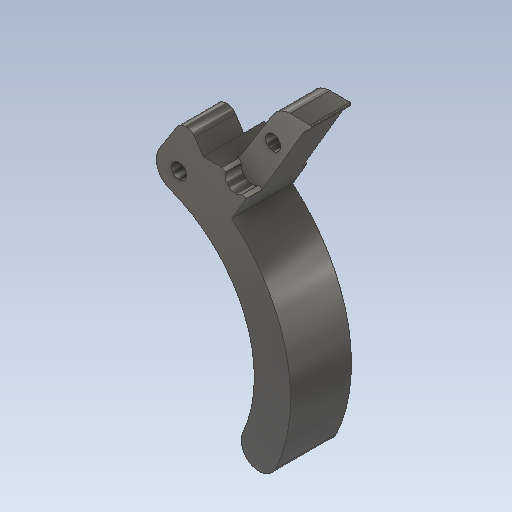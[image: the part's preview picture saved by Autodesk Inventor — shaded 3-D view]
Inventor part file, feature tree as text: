
AUTODESK INVENTOR PART (.ipt)
format: ipt  version: 2021 (Build 250183000, 183)  size: 243,712 bytes
history: native  units: in
note: dims shown in document units (in); Inventor stores cm internally (conversion verified against a paired STEP export)
features: extrude x8, sketch x8, projected_geometry x6, fillet x1
ambient origin geometry x8: Origin, YZ Plane, XZ Plane, XY Plane, X Axis, Y Axis, Z Axis, Center Point
bodies: Solid3 (feature_tree)
feature tree (23):
  extrude  "Extrusion12"  Depth=0.0787in
  extrude  "Extrusion13"  Depth=0.0591in
  extrude  "Extrusion17"  Depth=0.2756in TaperAngle=0.0deg
  extrude  "Extrusion18"  Depth=0.0787in
  extrude  "Extrusion19"  Depth=0.1026in TaperAngle=0.0deg
  extrude  "Extrusion20"  Depth=0.0394in TaperAngle=0.0deg
  extrude  "Extrusion22"  Depth=0.3937in TaperAngle=0.0deg
  fillet  "Fillet8"  Radius=0.0091in
  extrude  "Extrusion23"  Depth=0.0394in TaperAngle=0.0deg
  sketch  "Sketch1"  dims[d6=0.0787in d53=0.0787in]
  sketch  "Sketch14"  dims[d54=0.2756in d55=0.0in d56=0.0591in]
  sketch  "Sketch15"  dims[d57=0.0591in d58=0.2756in d59=0.0in]
  projected_geometry  "Projected Loop10"
  sketch  "Sketch18"  dims[d73=0.0787in d74=0.0in d75=0.0157in]
  projected_geometry  "Projected Loop11"
  sketch  "Sketch19"  dims[d76=0.0157in d77=0.1026in d78=0.0in]
  projected_geometry  "Projected Loop12"
  sketch  "Sketch20"  dims[d79=0.0197in d80=0.0394in d81=0.0in]
  projected_geometry  "Projected Loop13"
  sketch  "Sketch22"  dims[d91=0.0187in d92=0.0in d96=0.3937in d97=0.0in d99=0.0091in]
  projected_geometry  "Projected Loop14"
  sketch  "Sketch23"  dims[d100=0.0039in d101=0.0394in d102=0.0in]
  projected_geometry  "Projected Loop15"
